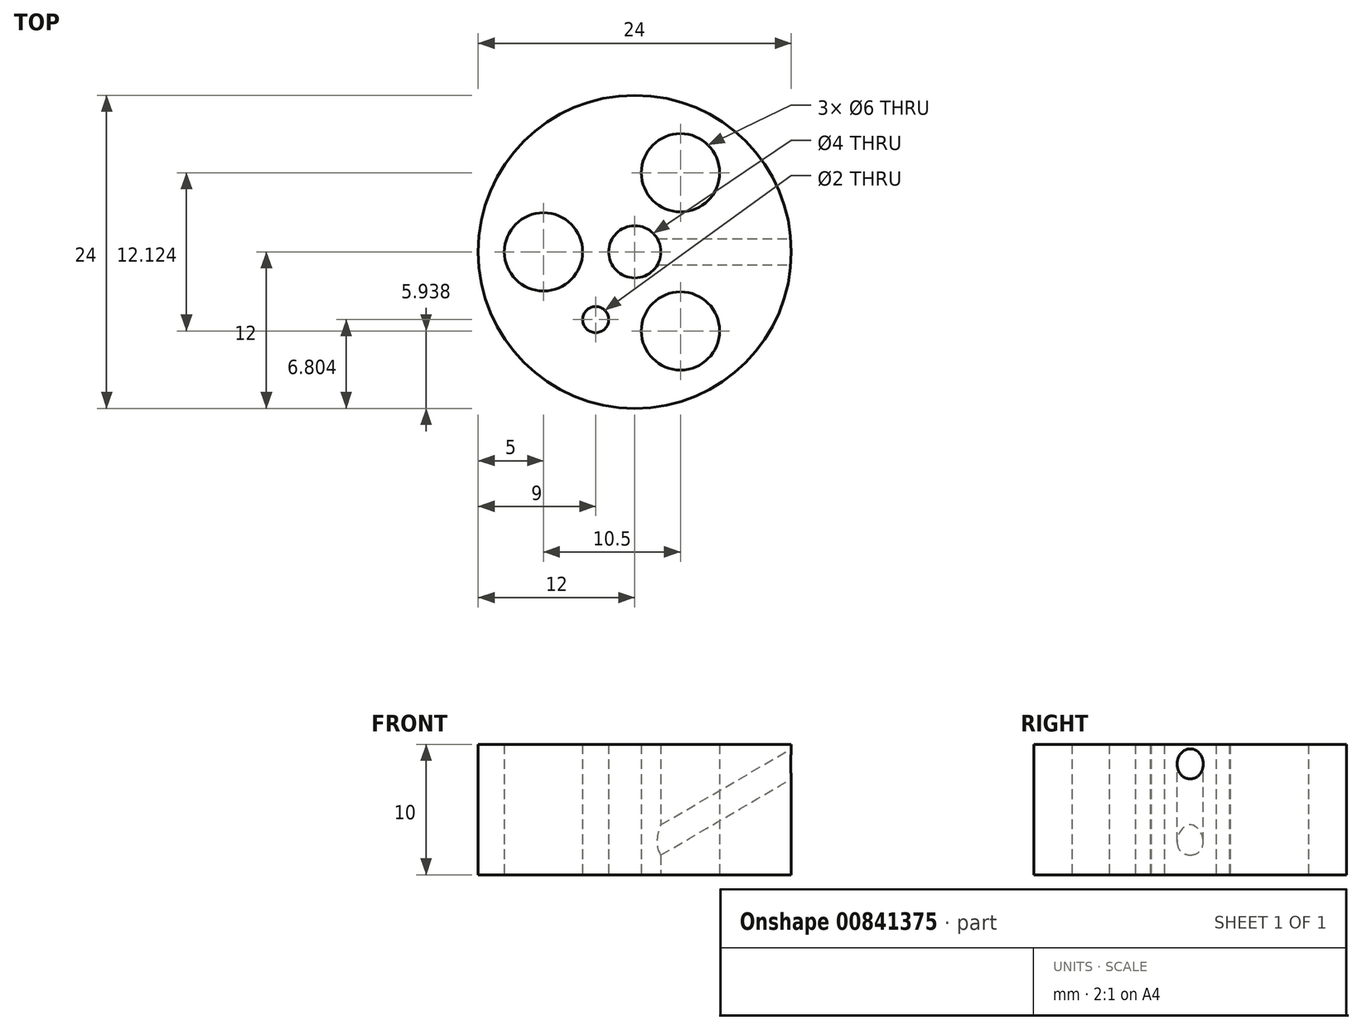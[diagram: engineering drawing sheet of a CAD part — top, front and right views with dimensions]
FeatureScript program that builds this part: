
annotation { "Feature Type Name" : "Feature", "Feature Type Description" : "" }
export const myFeature = defineFeature(function(context is Context, id is Id, definition is map)
    precondition{}
    {
        {
            var Q0;
            Q0=qCreatedBy(makeId("Front.planeOp"),FACE);
            var sketch = newSketch(context, id + "F0", { "sketchPlane" : qUnion([Q0])});
            skLineSegment(sketch, "E0", {"start": v(0, 0) * mm, "end": v(0, 14.18) * mm, "construction": true});
            skLineSegment(sketch, "E1.bottom", {"start": v(2, 0) * mm, "end": v(12, 0) * mm});
            skLineSegment(sketch, "E1.top", {"start": v(2, 10) * mm, "end": v(12, 10) * mm});
            skLineSegment(sketch, "E1.left", {"start": v(2, 0) * mm, "end": v(2, 10) * mm});
            skLineSegment(sketch, "E1.right", {"start": v(12, 0) * mm, "end": v(12, 10) * mm});
            skSolve(sketch);
        }
        {
            var Q0;
            Q0 = qSketchRegion(id + "F0", true);
            var Q1;
            Q1=sQuery(id+"F0.wireOp",EDGE,"E0");
            revolve(context, id + "F1", {"surfaceOperationType" : NewSurfaceOperationType.NEW, "entities" : qUnion([Q0]), "axis" : qUnion([Q1]), "revolveType" : RevolveType.FULL});
        }
        {
            var Q0;
            Q0=qCreatedBy(makeId("Front.planeOp"),FACE);
            var sketch = newSketch(context, id + "F2", { "sketchPlane" : qUnion([Q0])});
            skLineSegment(sketch, "E2", {"start": v(0, 1.5) * mm, "end": v(12.58, 8.84) * mm});
            skLineSegment(sketch, "E3", {"start": v(12.58, 8.84) * mm, "end": v(13.08, 7.97) * mm});
            skLineSegment(sketch, "E4", {"start": v(13.08, 7.97) * mm, "end": v(0.5, 0.64) * mm});
            skLineSegment(sketch, "E5", {"start": v(0.5, 0.64) * mm, "end": v(0, 1.5) * mm});
            skLineSegment(sketch, "E6", {"start": v(12.58, 8.84) * mm, "end": v(16.24, 10.97) * mm, "construction": true});
            skPoint(sketch, "E7", {"position": v(12, 8.5) * mm});
            skSolve(sketch);
        }
        {
            var Q0;
            Q0 = qSketchRegion(id + "F2", true);
            var Q1;
            Q1=sQuery(id+"F2.wireOp",EDGE,"E6");
            revolve(context, id + "F3", {"operationType" : NewBodyOperationType.REMOVE, "surfaceOperationType" : NewSurfaceOperationType.NEW, "entities" : qUnion([Q0]), "axis" : qUnion([Q1]), "revolveType" : RevolveType.FULL, "oppositeDirection" : true});
        }
        {
            var Q0;
            Q0=qCreatedBy(makeId("Top.planeOp"),FACE);
            var sketch = newSketch(context, id + "F4", { "sketchPlane" : qUnion([Q0])});
            skCircle(sketch, "E8", {"center": v(3.5, 6.06) * mm, "radius": 3 * mm});
            skCircle(sketch, "E9", {"center": v(-3, -5.2) * mm, "radius": 1 * mm});
            skCircle(sketch, "E10.1.0", {"center": v(-7, 0) * mm, "radius": 3 * mm});
            skCircle(sketch, "E10.2.0", {"center": v(3.5, -6.06) * mm, "radius": 3 * mm});
            skPoint(sketch, "E10.center", {"position": v(0, 0) * mm});
            skLineSegment(sketch, "E11", {"start": v(0, 0) * mm, "end": v(0, 11.47) * mm, "construction": true});
            skLineSegment(sketch, "E12", {"start": v(3.5, 6.06) * mm, "end": v(0, 0) * mm, "construction": true});
            skSolve(sketch);
        }
        {
            var Q0;
            Q0 = qSketchRegion(id + "F4", true);
            extrude(context, id + "F5", {"entities" : qUnion([Q0]), "operationType" : NewBodyOperationType.REMOVE, "endBound" : BoundingType.THROUGH_ALL, "depth" : 25 * mm, "offsetDistance" : 25 * mm});
        }
    });
